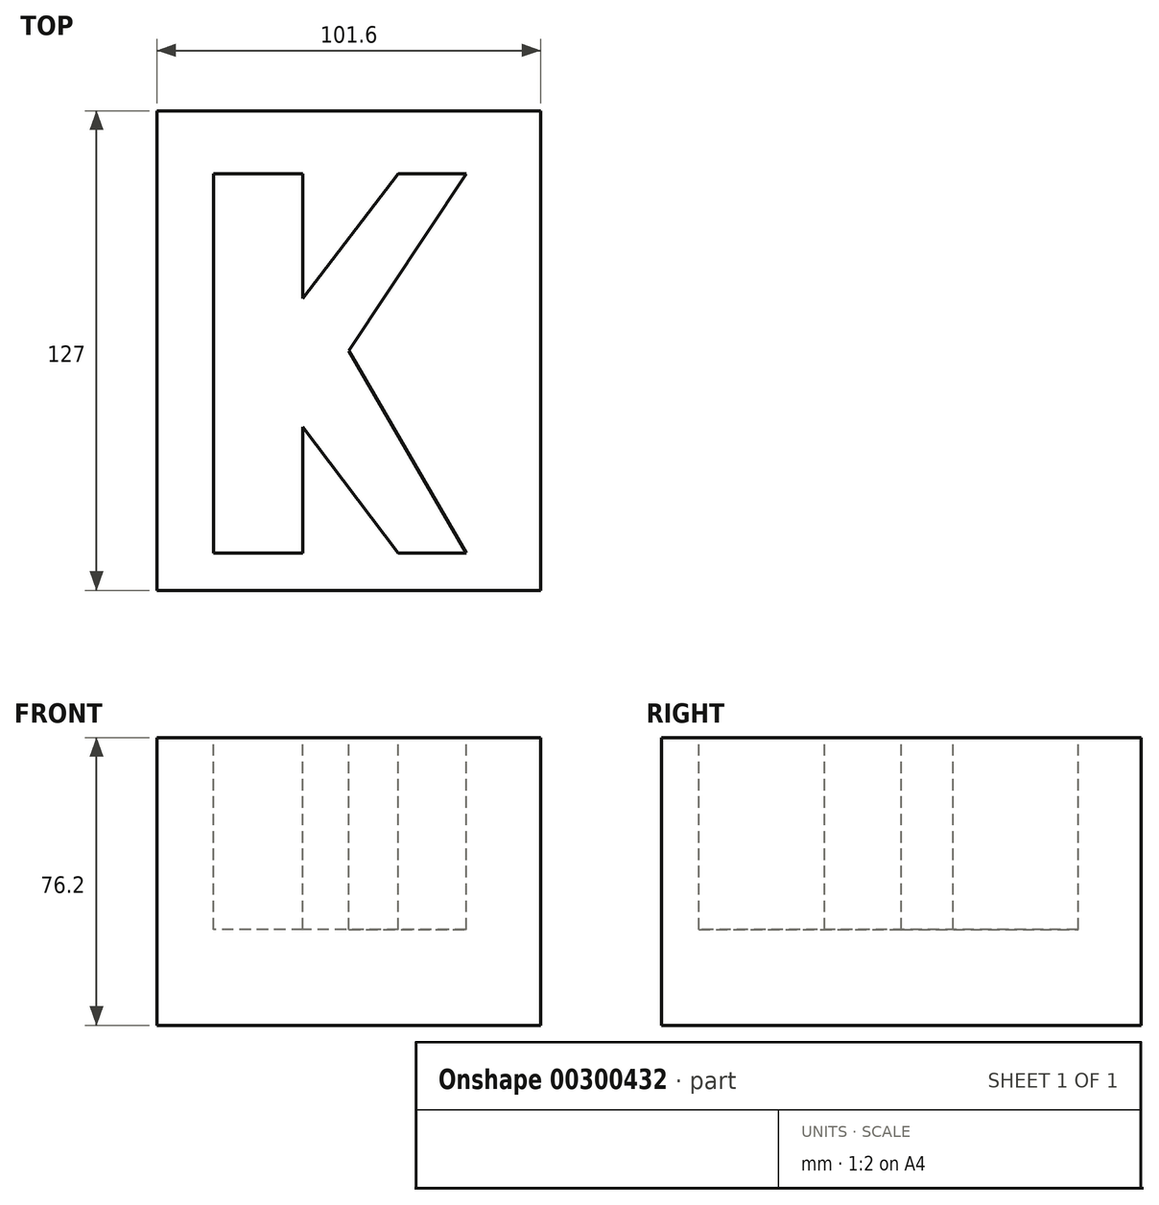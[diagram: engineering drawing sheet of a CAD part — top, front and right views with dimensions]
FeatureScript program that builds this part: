
annotation { "Feature Type Name" : "Feature", "Feature Type Description" : "" }
export const myFeature = defineFeature(function(context is Context, id is Id, definition is map)
    precondition{}
    {
        {
            var Q0;
            Q0=qCreatedBy(makeId("Top.planeOp"),FACE);
            var sketch = newSketch(context, id + "F0", { "sketchPlane" : qUnion([Q0])});
            skLineSegment(sketch, "E0.bottom", {"start": v(-50.8, 63.5) * mm, "end": v(50.8, 63.5) * mm});
            skLineSegment(sketch, "E0.top", {"start": v(-50.8, -63.5) * mm, "end": v(50.8, -63.5) * mm});
            skLineSegment(sketch, "E0.left", {"start": v(-50.8, 63.5) * mm, "end": v(-50.8, -63.5) * mm});
            skLineSegment(sketch, "E0.right", {"start": v(50.8, 63.5) * mm, "end": v(50.8, -63.5) * mm});
            skPoint(sketch, "E0.middle", {"position": v(0, 0) * mm});
            skSolve(sketch);
        }
        {
            var Q0;
            Q0=makeQuery(id+"F0.imprint","IMPRINT",FACE,{"disambiguationData":[TD([[makeQuery(id+"F0.imprint","IMPRINT",EDGE,{"derivedFrom":sQuery(id+"F0.wireOp",EDGE,"E0.bottom")}),-1.0]])]});
            extrude(context, id + "F1", {"entities" : qUnion([Q0]), "depth" : 76.2 * mm});
        }
        {
            var Q0;
            Q0=makeQuery(id+"F1.opExtrude","CAP_FACE",FACE,{"disambiguationData":[OSD([sQuery(id+"F0.wireOp",EDGE,"E0.bottom"),sQuery(id+"F0.wireOp",EDGE,"E0.top"),sQuery(id+"F0.wireOp",EDGE,"E0.left"),sQuery(id+"F0.wireOp",EDGE,"E0.right")])],"isStart":false});
            var sketch = newSketch(context, id + "F2", { "sketchPlane" : qUnion([Q0])});
            skLineSegment(sketch, "E1", {"start": v(-35.76, 46.83) * mm, "end": v(-35.76, -53.65) * mm});
            skLineSegment(sketch, "E2", {"start": v(-35.76, -53.65) * mm, "end": v(-12.17, -53.65) * mm});
            skLineSegment(sketch, "E3", {"start": v(-12.17, -53.65) * mm, "end": v(-12.17, -20.28) * mm});
            skLineSegment(sketch, "E4", {"start": v(0, 0) * mm, "end": v(31.08, 46.83) * mm});
            skLineSegment(sketch, "E5", {"start": v(31.08, 46.83) * mm, "end": v(13.11, 46.83) * mm});
            skLineSegment(sketch, "E6", {"start": v(13.11, 46.83) * mm, "end": v(-12.17, 13.75) * mm});
            skLineSegment(sketch, "E7", {"start": v(-12.17, 13.75) * mm, "end": v(-12.17, 46.83) * mm});
            skLineSegment(sketch, "E8", {"start": v(-12.17, 46.83) * mm, "end": v(-35.76, 46.83) * mm});
            skLineSegment(sketch, "E9", {"start": v(-12.17, -20.28) * mm, "end": v(13.11, -53.65) * mm});
            skLineSegment(sketch, "E10", {"start": v(13.11, -53.65) * mm, "end": v(31.08, -53.65) * mm});
            skLineSegment(sketch, "E11", {"start": v(31.08, -53.65) * mm, "end": v(0, 0) * mm});
            skSolve(sketch);
        }
        {
            var Q0;
            Q0=makeQuery(id+"F2.imprint","IMPRINT",FACE,{"disambiguationData":[TD([[makeQuery(id+"F2.imprint","IMPRINT",EDGE,{"derivedFrom":sQuery(id+"F2.wireOp",EDGE,"E1")}),1.0]])]});
            extrude(context, id + "F3", {"entities" : qUnion([Q0]), "operationType" : NewBodyOperationType.REMOVE, "oppositeDirection" : true, "depth" : 50.8 * mm});
        }
    });
